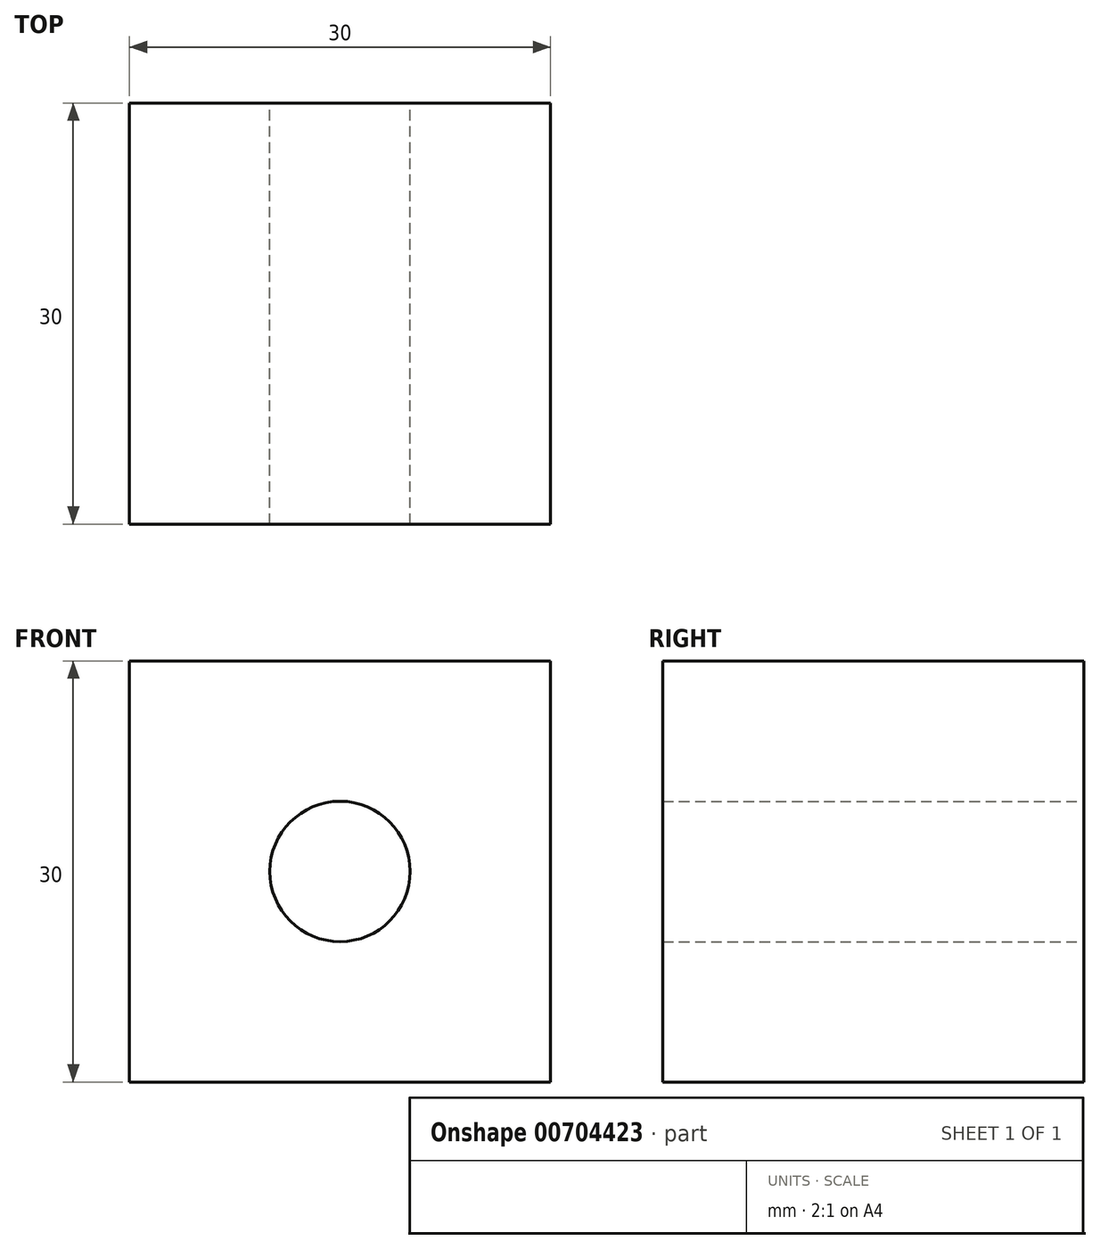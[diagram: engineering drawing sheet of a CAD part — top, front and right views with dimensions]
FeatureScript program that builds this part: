
annotation { "Feature Type Name" : "Feature", "Feature Type Description" : "" }
export const myFeature = defineFeature(function(context is Context, id is Id, definition is map)
    precondition{}
    {
        {
            var Q0;
            Q0=qCreatedBy(makeId("Top.planeOp"),FACE);
            var sketch = newSketch(context, id + "F0", { "sketchPlane" : qUnion([Q0])});
            skLineSegment(sketch, "E0.bottom", {"start": v(-15, 15) * mm, "end": v(15, 15) * mm});
            skLineSegment(sketch, "E0.top", {"start": v(-15, -15) * mm, "end": v(15, -15) * mm});
            skLineSegment(sketch, "E0.left", {"start": v(-15, 15) * mm, "end": v(-15, -15) * mm});
            skLineSegment(sketch, "E0.right", {"start": v(15, 15) * mm, "end": v(15, -15) * mm});
            skPoint(sketch, "E0.middle", {"position": v(0, 0) * mm});
            skSolve(sketch);
        }
        {
            var Q0;
            Q0 = qSketchRegion(id + "F0", true);
            extrude(context, id + "F1", {"entities" : qUnion([Q0]), "depth" : 30 * mm, "offsetDistance" : 25 * mm});
        }
        {
            var Q0;
            Q0=makeQuery(id+"F1.opExtrude","SWEPT_FACE",FACE,{"disambiguationData":[OSD([sQuery(id+"F0.wireOp",EDGE,"E0.bottom")])]});
            var sketch = newSketch(context, id + "F2", { "sketchPlane" : qUnion([Q0])});
            skCircle(sketch, "E1", {"center": v(0, 15) * mm, "radius": 5 * mm});
            skPoint(sketch, "E2", {"position": v(-15, 15) * mm});
            skSolve(sketch);
        }
        {
            var Q0;
            Q0=makeQuery(id+"F2.imprint","IMPRINT",FACE,{"disambiguationData":[TD([[makeQuery(id+"F2.imprint","IMPRINT",EDGE,{"derivedFrom":sQuery(id+"F2.wireOp",EDGE,"E1")}),1.0]])]});
            extrude(context, id + "F3", {"entities" : qUnion([Q0]), "operationType" : NewBodyOperationType.REMOVE, "endBound" : BoundingType.THROUGH_ALL, "oppositeDirection" : true, "depth" : 25 * mm, "offsetDistance" : 25 * mm});
        }
    });
